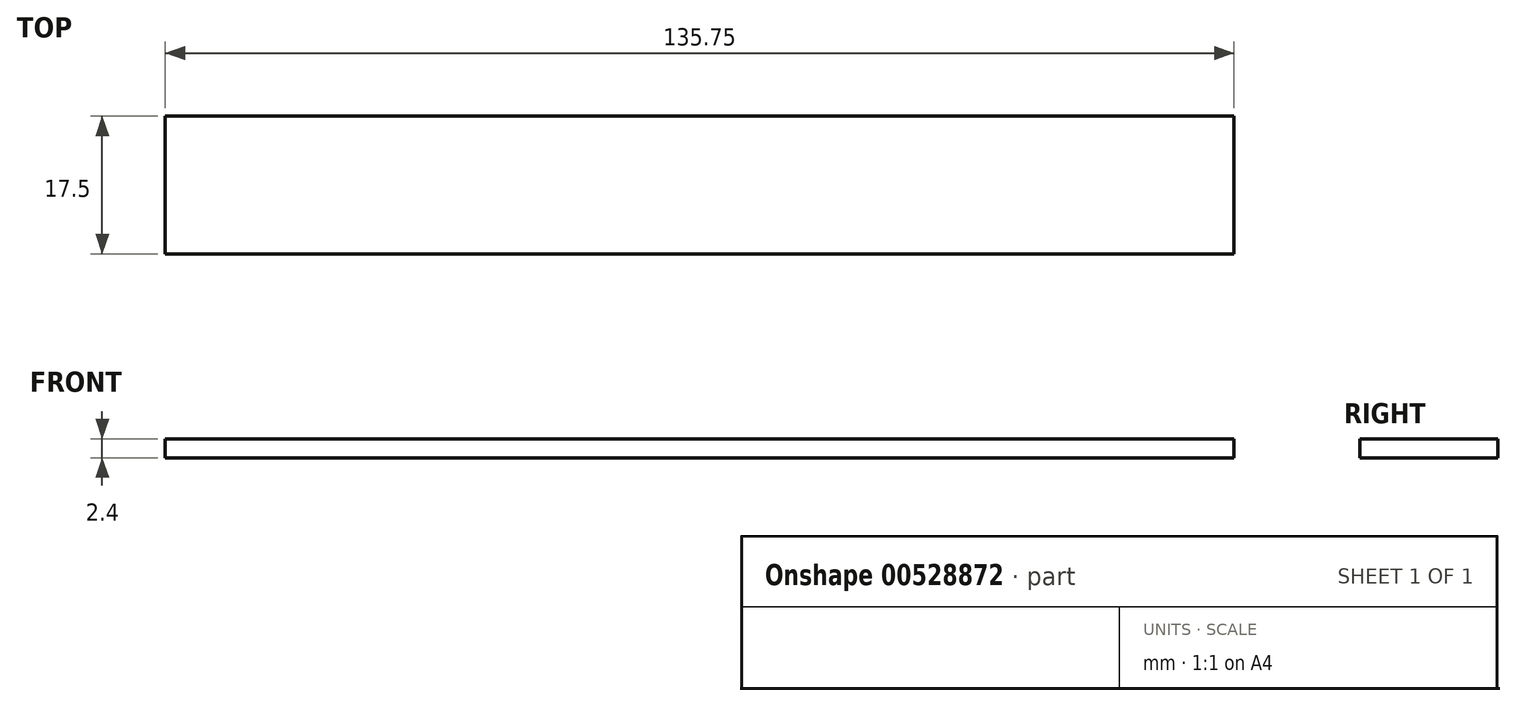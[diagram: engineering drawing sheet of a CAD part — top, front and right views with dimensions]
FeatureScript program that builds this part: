
annotation { "Feature Type Name" : "Feature", "Feature Type Description" : "" }
export const myFeature = defineFeature(function(context is Context, id is Id, definition is map)
    precondition{}
    {
        {
            var Q0;
            Q0=qCreatedBy(makeId("Top.planeOp"),FACE);
            var sketch = newSketch(context, id + "F0", { "sketchPlane" : qUnion([Q0])});
            skLineSegment(sketch, "E0.bottom", {"start": v(-66.23, -0.38) * mm, "end": v(69.52, -0.38) * mm});
            skLineSegment(sketch, "E0.top", {"start": v(-66.23, -17.88) * mm, "end": v(69.52, -17.88) * mm});
            skLineSegment(sketch, "E0.left", {"start": v(-66.23, -0.38) * mm, "end": v(-66.23, -17.88) * mm});
            skLineSegment(sketch, "E0.right", {"start": v(69.52, -0.38) * mm, "end": v(69.52, -17.88) * mm});
            skSolve(sketch);
        }
        {
            var Q0;
            Q0=makeQuery(id+"F0.imprint","IMPRINT",FACE,{"disambiguationData":[TD([[makeQuery(id+"F0.imprint","IMPRINT",EDGE,{"derivedFrom":sQuery(id+"F0.wireOp",EDGE,"E0.bottom")}),-1.0]])]});
            extrude(context, id + "F1", {"entities" : qUnion([Q0]), "depth" : 2.4 * mm, "offsetDistance" : 25.4 * mm});
        }
    });
